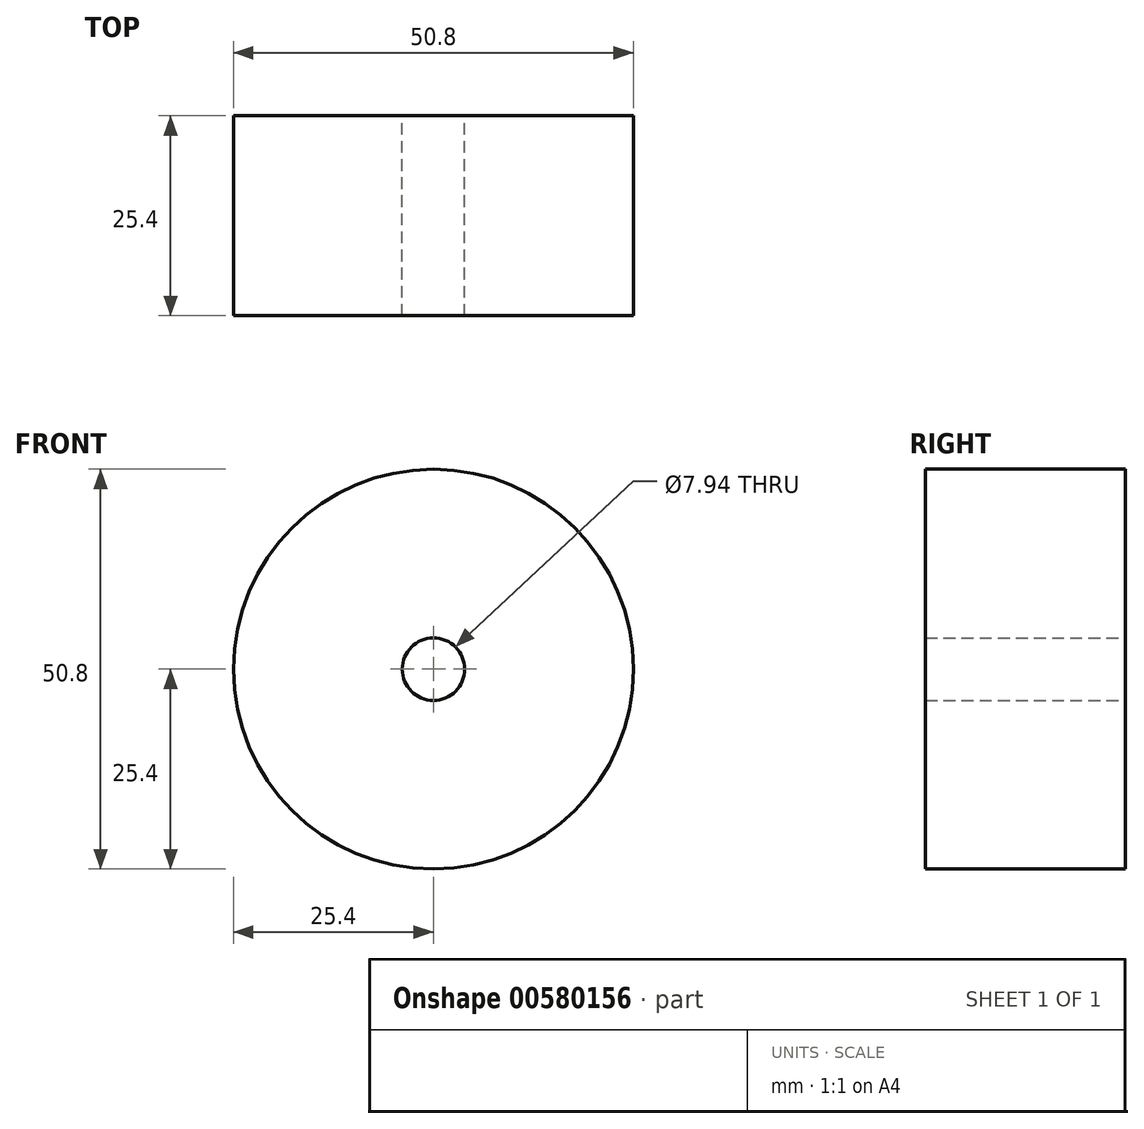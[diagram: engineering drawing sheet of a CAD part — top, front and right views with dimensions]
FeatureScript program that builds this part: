
annotation { "Feature Type Name" : "Feature", "Feature Type Description" : "" }
export const myFeature = defineFeature(function(context is Context, id is Id, definition is map)
    precondition{}
    {
        {
            var Q0;
            Q0=qCreatedBy(makeId("Front.planeOp"),FACE);
            var sketch = newSketch(context, id + "F0", { "sketchPlane" : qUnion([Q0])});
            skCircle(sketch, "E0", {"center": v(0, 0) * mm, "radius": 25.4 * mm});
            skCircle(sketch, "E1", {"center": v(0, 0) * mm, "radius": 3.97 * mm});
            skSolve(sketch);
        }
        {
            var Q0;
            Q0=qSketchRegion(id+"F0",true);
            extrude(context, id + "F1", {"entities" : qUnion([Q0]), "depth" : 25.4 * mm, "symmetric" : true});
        }
    });
